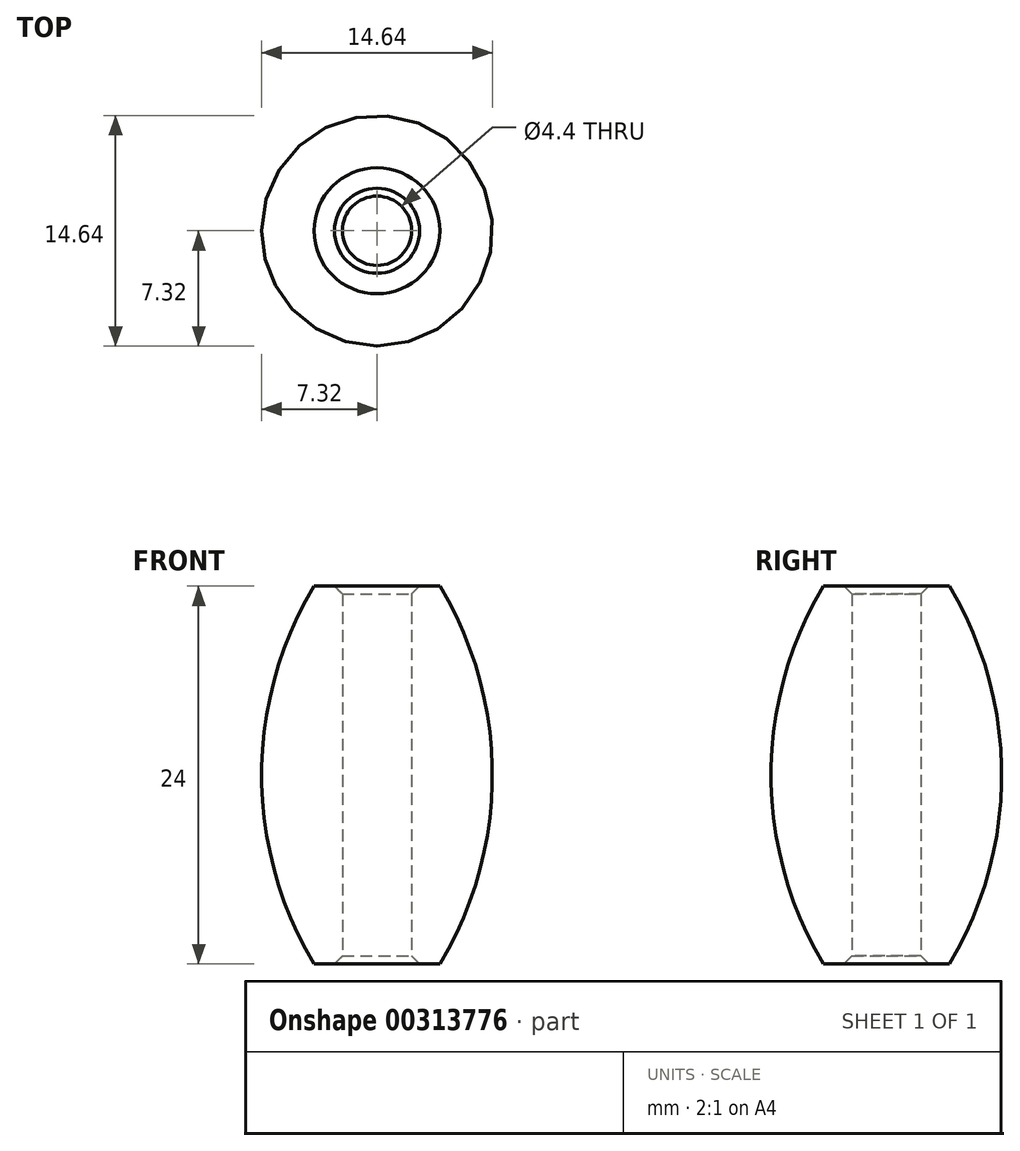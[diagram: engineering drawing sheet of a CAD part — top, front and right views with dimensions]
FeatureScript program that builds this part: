
annotation { "Feature Type Name" : "Feature", "Feature Type Description" : "" }
export const myFeature = defineFeature(function(context is Context, id is Id, definition is map)
    precondition{}
    {
        {
            var Q0;
            Q0=qCreatedBy(makeId("Front.planeOp"),FACE);
            var sketch = newSketch(context, id + "F0", { "sketchPlane" : qUnion([Q0])});
            skLineSegment(sketch, "E0", {"start": v(0, 0) * mm, "end": v(0, 24) * mm, "construction": true});
            skLineSegment(sketch, "E1", {"start": v(2.2, 0) * mm, "end": v(2.2, 24) * mm});
            skLineSegment(sketch, "E2", {"start": v(2.2, 24) * mm, "end": v(4, 24) * mm});
            skLineSegment(sketch, "E3", {"start": v(2.2, 0) * mm, "end": v(4, 0) * mm});
            skLineSegment(sketch, "E4", {"start": v(4, 24) * mm, "end": v(4, 0) * mm, "construction": true});
            skArc(sketch, "E5", {"start": v(4, 0) * mm, "mid": v(7.32, 12) * mm, "end": v(4, 24) * mm});
            skSolve(sketch);
        }
        {
            var Q0;
            Q0=qSketchRegion(id+"F0",true);
            var Q1;
            Q1=sQuery(id+"F0.wireOp",EDGE,"E0");
            revolve(context, id + "F1", {"entities" : qUnion([Q0]), "axis" : qUnion([Q1]), "revolveType" : RevolveType.FULL});
        }
        {
            var Q0;
            Q0=makeQuery(id+"F1.opRevolve","SWEPT_EDGE",EDGE,{"disambiguationData":[OSD([sQuery(id+"F0.wireOp",EDGE,"E1"),sQuery(id+"F0.wireOp",EDGE,"E2")])]});
            var Q1;
            Q1=makeQuery(id+"F1.opRevolve","SWEPT_EDGE",EDGE,{"disambiguationData":[OSD([sQuery(id+"F0.wireOp",EDGE,"E1"),sQuery(id+"F0.wireOp",EDGE,"E3")])]});
            chamfer(context, id + "F2", {"entities" : qUnion([Q0, Q1]), "width" : 0.5 * mm, "tangentPropagation" : true});
        }
    });
